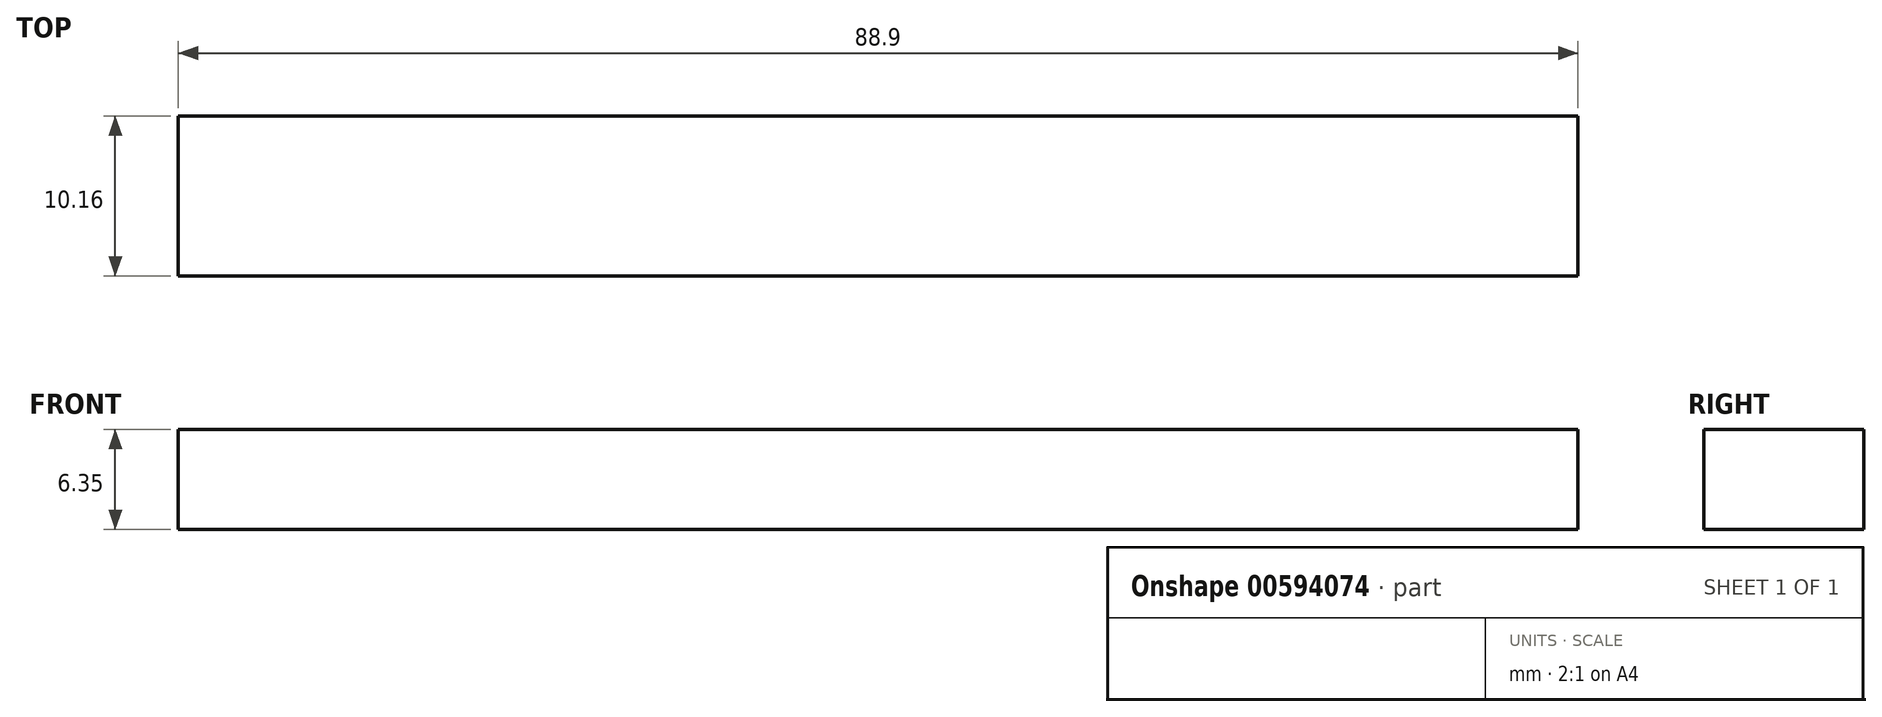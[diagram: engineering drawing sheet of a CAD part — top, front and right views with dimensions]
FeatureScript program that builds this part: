
annotation { "Feature Type Name" : "Feature", "Feature Type Description" : "" }
export const myFeature = defineFeature(function(context is Context, id is Id, definition is map)
    precondition{}
    {
        {
            var Q0;
            Q0=qCreatedBy(makeId("Top.planeOp"),FACE);
            var sketch = newSketch(context, id + "F0", { "sketchPlane" : qUnion([Q0])});
            skLineSegment(sketch, "E0.bottom", {"start": v(0, 0) * mm, "end": v(88.9, 0) * mm});
            skLineSegment(sketch, "E0.top", {"start": v(0, -10.16) * mm, "end": v(88.9, -10.16) * mm});
            skLineSegment(sketch, "E0.left", {"start": v(0, 0) * mm, "end": v(0, -10.16) * mm});
            skLineSegment(sketch, "E0.right", {"start": v(88.9, 0) * mm, "end": v(88.9, -10.16) * mm});
            skSolve(sketch);
        }
        {
            var Q0;
            Q0=makeQuery(id+"F0.imprint","IMPRINT",FACE,{"disambiguationData":[TD([[makeQuery(id+"F0.imprint","IMPRINT",EDGE,{"derivedFrom":sQuery(id+"F0.wireOp",EDGE,"E0.bottom")}),-1.0]])]});
            extrude(context, id + "F1", {"entities" : qUnion([Q0]), "depth" : 6.35 * mm, "offsetDistance" : 25.4 * mm});
        }
    });
